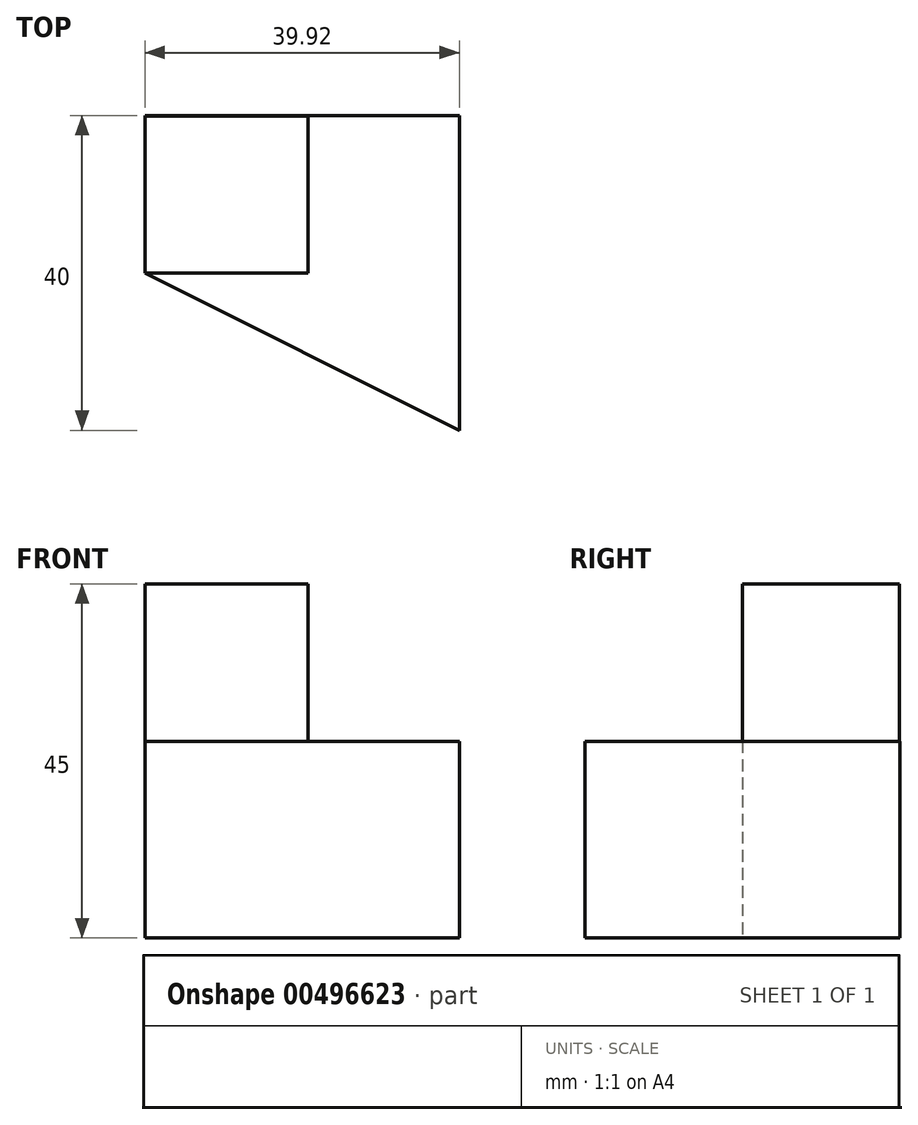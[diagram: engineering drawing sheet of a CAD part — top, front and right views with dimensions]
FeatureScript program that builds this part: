
annotation { "Feature Type Name" : "Feature", "Feature Type Description" : "" }
export const myFeature = defineFeature(function(context is Context, id is Id, definition is map)
    precondition{}
    {
        {
            var Q0;
            Q0=qCreatedBy(makeId("Top.planeOp"),FACE);
            var sketch = newSketch(context, id + "F0", { "sketchPlane" : qUnion([Q0])});
            skLineSegment(sketch, "E0", {"start": v(0, 0) * mm, "end": v(0, 20) * mm});
            skLineSegment(sketch, "E1", {"start": v(0, 20) * mm, "end": v(39.92, 20) * mm});
            skLineSegment(sketch, "E2", {"start": v(39.92, 20) * mm, "end": v(39.92, -20) * mm});
            skLineSegment(sketch, "E3", {"start": v(39.92, -20) * mm, "end": v(0, 0) * mm});
            skSolve(sketch);
        }
        {
            var Q0;
            Q0=qCreatedBy(makeId("Top.planeOp"),FACE);
            var sketch = newSketch(context, id + "F1", { "sketchPlane" : qUnion([Q0])});
            skLineSegment(sketch, "E4", {"start": v(0, 0) * mm, "end": v(20.7, 0) * mm});
            skLineSegment(sketch, "E5", {"start": v(20.7, 0) * mm, "end": v(20.7, 19.92) * mm});
            skLineSegment(sketch, "E6", {"start": v(20.7, 19.92) * mm, "end": v(0, 19.92) * mm});
            skLineSegment(sketch, "E7", {"start": v(0, 19.92) * mm, "end": v(0, 0) * mm});
            skSolve(sketch);
        }
        {
            var Q0;
            Q0=makeQuery(id+"F0.imprint","IMPRINT",FACE,{"disambiguationData":[TD([[makeQuery(id+"F0.imprint","IMPRINT",EDGE,{"derivedFrom":sQuery(id+"F0.wireOp",EDGE,"E0")}),-1.0]])]});
            extrude(context, id + "F2", {"entities" : qUnion([Q0]), "depth" : 25 * mm});
        }
        {
            var Q0;
            Q0=makeQuery(id+"F1.imprint","IMPRINT",FACE,{"disambiguationData":[TD([[makeQuery(id+"F1.imprint","IMPRINT",EDGE,{"derivedFrom":sQuery(id+"F1.wireOp",EDGE,"E4")}),1.0]])]});
            extrude(context, id + "F3", {"entities" : qUnion([Q0]), "operationType" : NewBodyOperationType.ADD, "depth" : 45 * mm});
        }
    });
